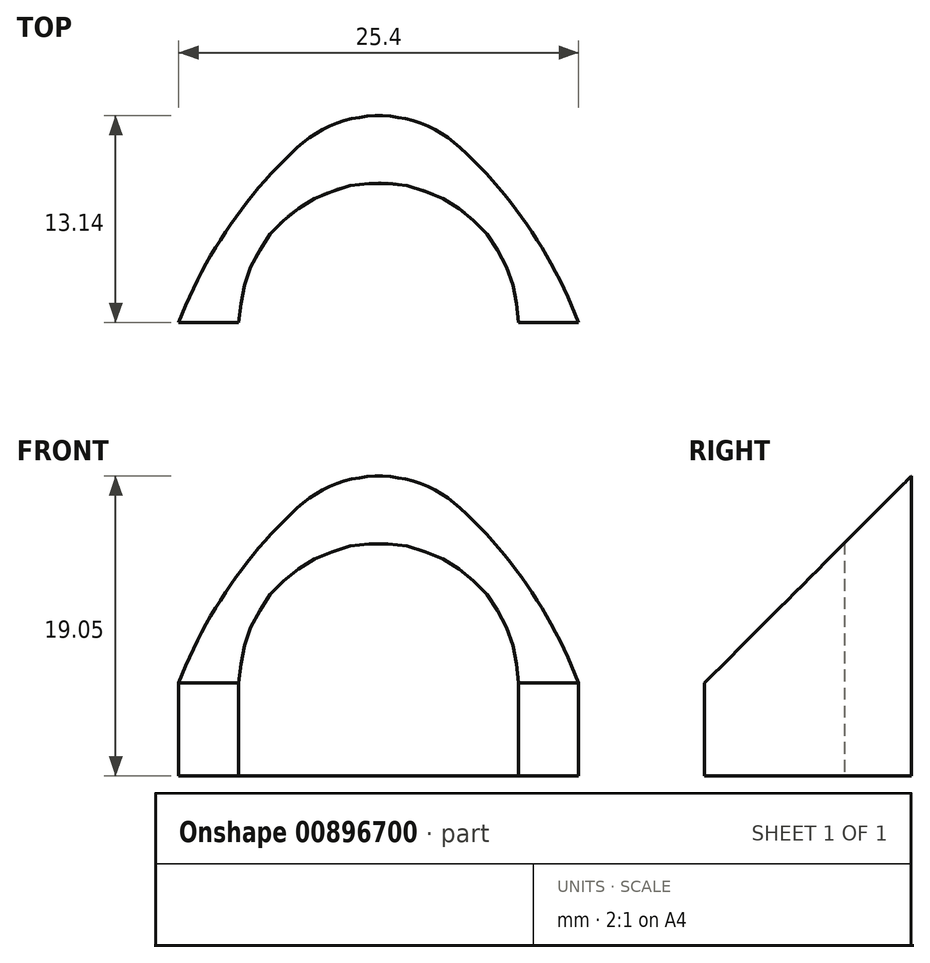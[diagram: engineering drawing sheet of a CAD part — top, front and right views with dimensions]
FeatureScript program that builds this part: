
annotation { "Feature Type Name" : "Feature", "Feature Type Description" : "" }
export const myFeature = defineFeature(function(context is Context, id is Id, definition is map)
    precondition{}
    {
        {
            var Q0;
            Q0=qCreatedBy(makeId("Top.planeOp"),FACE);
            var sketch = newSketch(context, id + "F0", { "sketchPlane" : qUnion([Q0])});
            skCircle(sketch, "E0", {"center": v(0, 0) * mm, "radius": 8.9 * mm, "construction": true});
            skLineSegment(sketch, "E1", {"start": v(-12.7, 0) * mm, "end": v(12.7, 0) * mm, "construction": true});
            skLineSegment(sketch, "E2", {"start": v(0, 0) * mm, "end": v(0, 14.95) * mm, "construction": true});
            skArc(sketch, "E3", {"start": v(-5.18, 11.11) * mm, "mid": v(-9.58, 5.99) * mm, "end": v(-12.7, 0) * mm});
            skArc(sketch, "E4.MirrorCS", {"start": v(5.18, 11.11) * mm, "mid": v(9.58, 5.99) * mm, "end": v(12.7, 0) * mm});
            skLineSegment(sketch, "E5", {"start": v(-12.7, 0) * mm, "end": v(-8.9, 0) * mm});
            skLineSegment(sketch, "E6", {"start": v(12.7, 0) * mm, "end": v(8.9, 0) * mm});
            skArc(sketch, "E7", {"start": v(8.9, 0) * mm, "mid": v(0, 8.9) * mm, "end": v(-8.9, 0) * mm});
            skPoint(sketch, "E8.visualSharp", {"position": v(0, 14.95) * mm});
            skArc(sketch, "E8.filletArc", {"start": v(5.18, 11.11) * mm, "mid": v(0, 13.14) * mm, "end": v(-5.18, 11.11) * mm});
            skSolve(sketch);
        }
        {
            var Q0;
            Q0=makeQuery(id+"F0.imprint","IMPRINT",FACE,{"disambiguationData":[TD([[makeQuery(id+"F0.imprint","IMPRINT",EDGE,{"derivedFrom":sQuery(id+"F0.wireOp",EDGE,"E3")}),1.0]])]});
            extrude(context, id + "F1", {"entities" : qUnion([Q0]), "depth" : 19.05 * mm, "offsetDistance" : 25.4 * mm});
        }
        {
            var Q0;
            Q0=qCreatedBy(makeId("Right.planeOp"),FACE);
            var sketch = newSketch(context, id + "F2", { "sketchPlane" : qUnion([Q0])});
            skLineSegment(sketch, "E9", {"start": v(0, 0) * mm, "end": v(0, 5.9) * mm, "construction": true});
            skLineSegment(sketch, "E10", {"start": v(0, 5.9) * mm, "end": v(13.14, 19.05) * mm});
            skLineSegment(sketch, "E11", {"start": v(13.14, 19.05) * mm, "end": v(26.7, 29.86) * mm});
            skLineSegment(sketch, "E12", {"start": v(26.7, 29.86) * mm, "end": v(-16.57, 33.97) * mm});
            skLineSegment(sketch, "E13", {"start": v(-16.57, 33.97) * mm, "end": v(-13.97, 8.77) * mm});
            skLineSegment(sketch, "E14", {"start": v(-13.97, 8.77) * mm, "end": v(0, 5.9) * mm});
            skSolve(sketch);
        }
        {
            var Q0;
            Q0=makeQuery(id+"F2.imprint","IMPRINT",FACE,{"disambiguationData":[TD([[makeQuery(id+"F2.imprint","IMPRINT",EDGE,{"derivedFrom":sQuery(id+"F2.wireOp",EDGE,"E10")}),1.0]])]});
            extrude(context, id + "F3", {"entities" : qUnion([Q0]), "operationType" : NewBodyOperationType.REMOVE, "endBound" : BoundingType.THROUGH_ALL, "oppositeDirection" : true, "depth" : 25.4 * mm, "offsetDistance" : 25.4 * mm, "hasSecondDirection" : true, "secondDirectionBound" : SecondDirectionBoundingType.THROUGH_ALL, "secondDirectionOppositeDirection" : false, "secondDirectionDepth" : 25.4 * mm});
        }
    });
